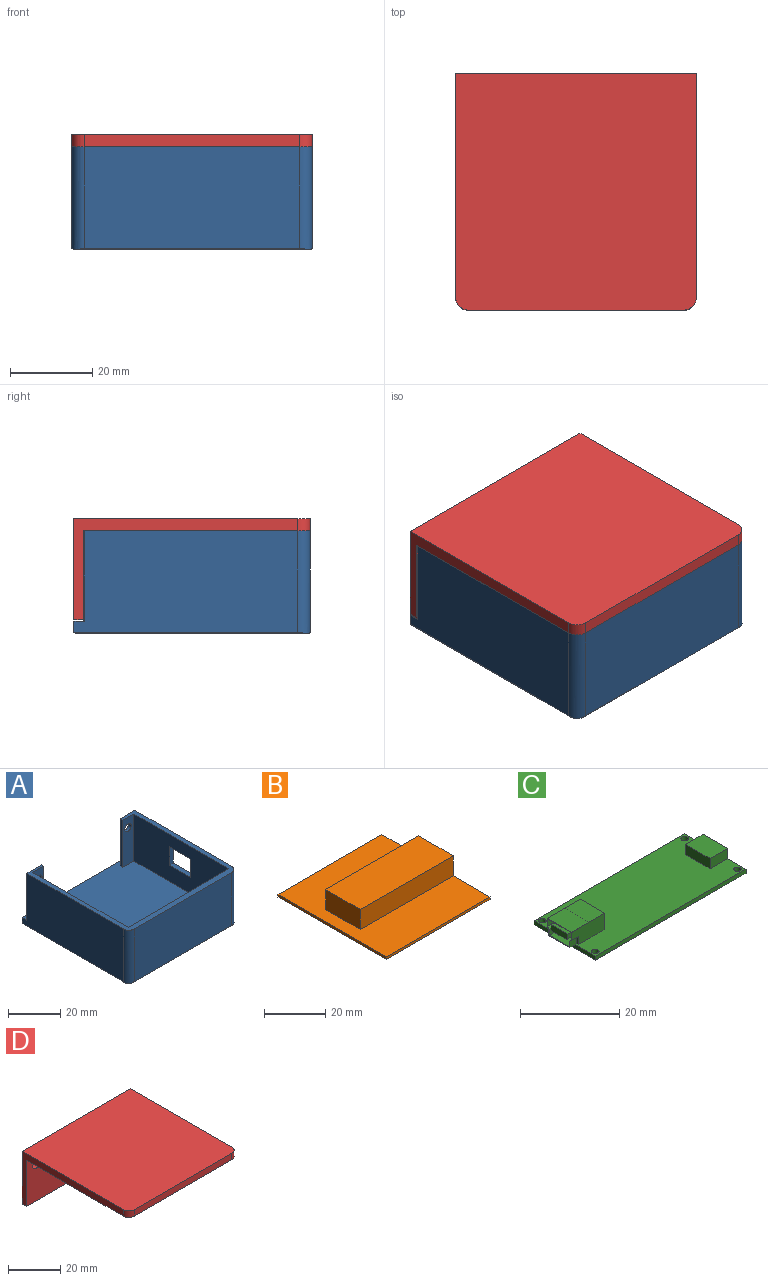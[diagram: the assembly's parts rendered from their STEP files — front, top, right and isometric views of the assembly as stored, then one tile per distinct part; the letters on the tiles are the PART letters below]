
ASSEMBLY  parts=4 mates=3
PART A: 28 faces, bbox 58.6x57.6x25 mm
  f0: plane 54.6x24.7mm, normal (1,0,0), area 1198.4mm2, adj f2,f4,f7,f15,f16,f17,f18,f19
  f1: plane 51.1x22mm, normal (-1,0,0), area 1025.3mm2, adj f2,f9,f10,f15,f16,f17,f18,f19
  f2: plane 58.6x55.27mm, normal (0,0,1), area 3002.5mm2, adj f0,f1,f4,f5,f7,f8,f9,f10
  f3: plane 52.6x24.7mm, normal (0,-1,0), area 1299.2mm2, adj f15,f23,f26,f27
  f4: plane 58.6x2.7mm, normal (0,1,0), area 158.2mm2, adj f0,f2,f5,f24
  f5: plane 54.6x24.7mm, normal (-1,0,0), area 1290mm2, adj f2,f4,f14,f15,f25,f27
  f6: plane 58x57mm, normal (0,0,-1), area 3304.5mm2, adj f22,f23,f24,f25,f26,f27
  f7: plane 22x8mm, normal (0,1,0), area 166.4mm2, adj f0,f2,f8,f15,f21
  f8: plane 22x1.5mm, normal (-1,0,0), area 33mm2, adj f2,f7,f9,f15
  f9: plane 22x6mm, normal (0,-1,0), area 122.4mm2, adj f1,f2,f8,f15,f21
  f10: plane 54.6x22mm, normal (-0.01,1,0), area 1201.2mm2, adj f1,f2,f11,f15
  f11: plane 51.43x22mm, normal (1,0,0), area 1131.5mm2, adj f2,f10,f12,f15
  f12: plane 22x6mm, normal (0,-1,0), area 122.4mm2, adj f2,f11,f13,f15,f20
  f13: plane 22x1.17mm, normal (1,0,0), area 25.7mm2, adj f2,f12,f14,f15
  f14: plane 22x8mm, normal (0,1,0), area 166.4mm2, adj f2,f5,f13,f15,f20
  f15: plane 58.6x55.27mm, normal (0,0,1), area 369mm2, adj f0,f1,f3,f5,f7,f8,f9,f10
  f16: plane 11.5x2mm, normal (0,0,1), area 23mm2, adj f0,f1,f17,f19
  f17: plane 8.6x2mm, normal (0,-1,0), area 17.2mm2, adj f0,f1,f16,f18
  f18: plane 11.5x2mm, normal (0,0,-1), area 23mm2, adj f0,f1,f17,f19
  f19: plane 8.6x2mm, normal (0,1,0), area 17.2mm2, adj f0,f1,f16,f18
  f20: cylinder r=1.75mm len=3.5mm, axis (0,1,0), area 12.9mm2, adj f12,f14
  f21: cylinder r=1.75mm len=3.5mm, axis (0,1,0), area 16.5mm2, adj f7,f9
  f22: plane 55.91x0.3mm, normal (0.71,0,-0.71), area 23.5mm2, adj f0,f6,f24,f26
  f23: plane 55.22x0.3mm, normal (0,-0.71,-0.71), area 23.1mm2, adj f3,f6,f26,f27
  f24: plane 58.6x0.3mm, normal (0,0.71,-0.71), area 24.7mm2, adj f4,f6,f22,f25
  f25: plane 55.91x0.3mm, normal (-0.71,0,-0.71), area 23.5mm2, adj f5,f6,f24,f27
  f26: cylinder r=3mm len=25mm, axis (0,0,1), area 117.3mm2, adj f0,f3,f6,f15,f22,f23
  f27: cylinder r=3mm len=25mm, axis (0,0,-1), area 117.3mm2, adj f3,f5,f6,f15,f23,f25
PART B: 10 faces, bbox 48x50x9 mm
  f0: plane 50x48mm, normal (0,0,1), area 1712mm2, adj f1,f2,f3,f4,f6,f7,f8
  f1: plane 48x1mm, normal (0,-1,0), area 48mm2, adj f0,f2,f4,f5
  f2: plane 50x9mm, normal (1,0,0), area 178mm2, adj f0,f1,f3,f5,f6,f8,f9
  f3: plane 48x1mm, normal (0,1,0), area 48mm2, adj f0,f2,f4,f5
  f4: plane 50x1mm, normal (-1,0,0), area 50mm2, adj f0,f1,f3,f5
  f5: plane 50x48mm, normal (0,0,-1), area 2400mm2, adj f1,f2,f3,f4
  f6: plane 43x8mm, normal (0,1,0), area 344mm2, adj f0,f2,f7,f9
  f7: plane 16x8mm, normal (-1,0,0), area 128mm2, adj f0,f6,f8,f9
  f8: plane 43x8mm, normal (0,-1,0), area 344mm2, adj f0,f2,f7,f9
  f9: plane 43x16mm, normal (0,0,1), area 688mm2, adj f2,f6,f7,f8
PART C: 42 faces, bbox 44.5x17.5x5 mm
  f0: plane 6x1.5mm, normal (0,0,-1), area 9mm2, adj f4,f12,f35,f37
  f1: plane 9.5x4mm, normal (0,1,0), area 34mm2, adj f2,f12,f14,f15,f38,f39
  f2: plane 43x17.5mm, normal (0,0,1), area 654.9mm2, adj f1,f3,f4,f5,f6,f7,f8,f9
  f3: plane 43x1mm, normal (0,1,0), area 43mm2, adj f2,f4,f9,f11
  f4: plane 17.5x1mm, normal (-1,0,0), area 17.5mm2, adj f0,f2,f3,f5,f11
  f5: plane 43x1mm, normal (0,-1,0), area 43mm2, adj f2,f4,f9,f11
  f6: cylinder r=0.75mm len=1.5mm, axis (0,0,1), area 4.7mm2, adj f2,f11
  f7: cylinder r=0.75mm len=1.5mm, axis (0,0,1), area 4.7mm2, adj f2,f11
  f8: cylinder r=0.75mm len=1.5mm, axis (0,0,1), area 4.7mm2, adj f2,f11
  f9: plane 17.5x3.5mm, normal (1,0,0), area 35mm2, adj f2,f3,f5,f11,f16,f18,f19
  f10: cylinder r=0.75mm len=1.5mm, axis (0,0,1), area 4.7mm2, adj f2,f11
  f11: plane 43x17.5mm, normal (0,0,-1), area 745.4mm2, adj f3,f4,f5,f6,f7,f8,f9,f10
  f12: plane 7x4mm, normal (-1,0,0), area 2.1mm2, adj f0,f1,f13,f15,f20,f21,f22,f23
  f13: plane 9.5x4mm, normal (0,-1,0), area 34mm2, adj f2,f12,f14,f15,f34,f36
  f14: plane 7x4mm, normal (1,0,0), area 28mm2, adj f1,f2,f13,f15
  f15: plane 9.5x7mm, normal (0,0,1), area 66.5mm2, adj f1,f12,f13,f14
  f16: plane 5x2.5mm, normal (0,1,0), area 12.5mm2, adj f2,f9,f17,f19
  f17: plane 7x2.5mm, normal (-1,0,0), area 17.5mm2, adj f2,f16,f18,f19
  f18: plane 5x2.5mm, normal (0,-1,0), area 12.5mm2, adj f2,f9,f17,f19
  f19: plane 7x5mm, normal (0,0,1), area 35mm2, adj f9,f16,f17,f18
  f20: plane 5.8x5mm, normal (0,0,1), area 29mm2, adj f12,f21,f31,f32
  f21: plane 5x1.44mm, normal (0,1,0), area 7.2mm2, adj f12,f20,f22,f32
  f22: plane 5x0.5mm, normal (0,0.71,0.71), area 3.5mm2, adj f12,f21,f23,f32
  f23: plane 5x1.86mm, normal (0,1,0), area 9.3mm2, adj f12,f22,f24,f32
  f24: plane 6.8x5mm, normal (0,0,-1), area 34mm2, adj f12,f23,f25,f32
  f25: plane 5x1.86mm, normal (0,-1,0), area 9.3mm2, adj f12,f24,f26,f32
  f26: plane 5x0.5mm, normal (0,-0.71,0.71), area 3.5mm2, adj f12,f25,f31,f32
  f27: plane 5x3.98mm, normal (0,0,-1), area 19.9mm2, adj f32,f33,f40,f41
  f28: plane 5x1.1mm, normal (0,1,0), area 5.5mm2, adj f29,f32,f33,f40
  f29: plane 5x4.78mm, normal (0,0,1), area 23.9mm2, adj f28,f30,f32,f33
  f30: plane 5x1.1mm, normal (0,-1,0), area 5.5mm2, adj f29,f32,f33,f41
  f31: plane 5x1.44mm, normal (0,-1,0), area 7.2mm2, adj f12,f20,f26,f32
  f32: plane 6.8x3.8mm, normal (-1,0,0), area 17.1mm2, adj f20,f21,f22,f23,f24,f25,f26,f27
  f33: plane 4.78x1.5mm, normal (-1,0,0), area 7mm2, adj f27,f28,f29,f30,f40,f41
  f34: plane 2x0.5mm, normal (0,-0.71,-0.71), area 1.4mm2, adj f12,f13,f35,f36
  f35: plane 2x1.5mm, normal (0,-1,0), area 3mm2, adj f0,f2,f12,f34,f36
  f36: plane 2x0.5mm, normal (-1,0,0), area 0.9mm2, adj f2,f13,f34,f35
  f37: plane 2x1.5mm, normal (0,1,0), area 3mm2, adj f0,f2,f12,f38,f39
  f38: plane 2x0.5mm, normal (0,0.71,-0.71), area 1.4mm2, adj f1,f12,f37,f39
  f39: plane 2x0.5mm, normal (-1,0,0), area 0.9mm2, adj f1,f2,f37,f38
  f40: plane 5x0.4mm, normal (0,0.71,-0.71), area 2.8mm2, adj f27,f28,f32,f33
  f41: plane 5x0.4mm, normal (0,-0.71,-0.71), area 2.8mm2, adj f27,f30,f32,f33
PART D: 13 faces, bbox 58.6x57.6x24.7 mm
  f0: plane 54.6x24.7mm, normal (1,0,0), area 213.7mm2, adj f1,f4,f5,f6,f7,f12
  f1: plane 58.6x24.7mm, normal (0,1,0), area 1305.5mm2, adj f0,f2,f4,f7,f8,f9,f10
  f2: plane 54.6x24.7mm, normal (-1,0,0), area 213.7mm2, adj f1,f4,f5,f6,f7,f11
  f3: plane 52.6x3mm, normal (0,-1,0), area 157.8mm2, adj f4,f5,f11,f12
  f4: plane 58.6x57.6mm, normal (0,0,1), area 3371.5mm2, adj f0,f1,f2,f3,f11,f12
  f5: plane 58.6x55.3mm, normal (0,0,-1), area 3236.7mm2, adj f0,f2,f3,f6,f11,f12
  f6: plane 58.6x21.7mm, normal (0,-1,0), area 1129.7mm2, adj f0,f2,f5,f7,f8,f9,f10
  f7: plane 58.6x2.3mm, normal (0,0,-1), area 134.8mm2, adj f0,f1,f2,f6
  f8: cylinder r=6.25mm len=12.5mm, axis (0,1,0), area 90.3mm2, adj f1,f6
  f9: cylinder r=1.75mm len=3.5mm, axis (0,1,0), area 25.3mm2, adj f1,f6
  f10: cylinder r=1.75mm len=3.5mm, axis (0,1,0), area 25.3mm2, adj f1,f6
  f11: cylinder r=3mm len=3mm, axis (0,0,1), area 14.1mm2, adj f2,f3,f4,f5
  f12: cylinder r=3mm len=3mm, axis (0,0,-1), area 14.1mm2, adj f0,f3,f4,f5
PLACE A t=(36.16,11.29,-31.32)mm
PLACE B t=(35.11,12.5,-28.32)mm
PLACE C rot(axis=(0,0,1),180deg) t=(37.61,12.5,-18.32)mm
PLACE D t=(35.16,11.29,-6.32)mm
MATE parallel A.f2 <-> B.f5  axis (0,0,1) through (35.11,12.5,-28.32)mm
MATE parallel D.f5 <-> A.f15  axis (0,0,-1) through (35.16,-17.51,-6.32)mm
MATE parallel C.f11 <-> B.f9  axis (0,0,-1) through (59.11,12.5,-19.32)mm
